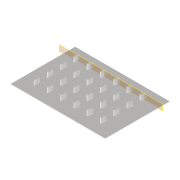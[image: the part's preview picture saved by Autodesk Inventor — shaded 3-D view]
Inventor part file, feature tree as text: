
AUTODESK INVENTOR PART (.ipt)
format: ipt  version: 2022 (Build 260153000, 153)  size: 3,486,208 bytes
history: native  units: mm
features: extrude x2, sketch x2, pattern_linear x1, plane x1, projected_geometry x1
ambient origin geometry x8: Origin, YZ Plane, XZ Plane, XY Plane, X Axis, Y Axis, Z Axis, Center Point
bodies: Volumenkörper1 (feature_tree)
feature tree (7):
  extrude  "Extrusion1"  Depth=1.0mm
  extrude  "Extrusion2"  Depth=8.55mm
  pattern_linear  "Rechteckige Anordnung1"  Spacing1=4.275mm  [1 undecoded]
  plane  "Arbeitsebene1"
  sketch  "Skizze5"  dims[d2=1.0mm d3=0.0mm d4=8.1mm]
  sketch  "Skizze6"  dims[d5=2.2mm d6=8.55mm d7=4.275mm d8=7.0mm d9=0.0mm d10=40.0mm d12=18.7mm d13=60.0mm d15=18.7mm]
  projected_geometry  "Projizierte Kontur1"
note: 1 required parameter value undecoded (feature->parameter linkage not recoverable at this tier; creation-order binding heuristic only, values carry confidence <= 0.55)
